# Revit family: Hager-IC-IP40-Transparent_Door-syst-PL-en
name_source: partatom
category: Electrical Equipment
units: mm (PartAtom-declared; Revit-internal decimal feet)

## family parameters
Cut with Voids When Loaded = No
Host = Face
Panel Configuration = Two Columns, Circuits Across
Part Type = Panelboard
Room Calculation Point = No
Round Connector Dimension = Use Diameter
Shared = No

## types (2) — shared parameters
EF000007 - Colour = EV000202 - White
EF000116 - RAL-number = 9010
EF000118 - With mounting plate = No
EF000266 - Number of rows = 2
EF000339 - Type of cover = EV004216 - Door
EF001062 - EMC-version = No
EF001088 - Extension possible = Yes
EF001131 - Internal depth = 72 mm  [stored 0.23622 ft]
EF001134 - DIN-rail = Yes
EF001596 - Material housing = EV000139 - Plastic
EF002950 - Width in number of modular spacings = 12
EF004462 - Type of closure = EV000154 - Other
EF005474 - Degree of protection (IP) = EV006415 - IP40
EF006244 - Transparent cover/door = Yes
EF006306 - With lock = No
EF009212 - Cover model = EV000116 - Closed
EF015776 - Earthing terminal block = Yes
EF015777 - Neutral terminal block = Yes
EF015941 - Signal passing door = Yes
HG000001 - Number of columns = 1
HG000002 - With door or cover = Yes
HG000003 - Range = IC
HG000005 - Thickness = 3 mm  [stored 0.00984252 ft]
HG000009 - Double swing door = No
HG000010 - Asymmetric doors = No
HG000011 - Empty rows from bottom = No
HG000017 - Distance between poles = 18 mm  [stored 0.0590551 ft]
Manufacturer = Hager
Type Comments = IC
zero-valued in all types: Default Elevation, HG000007 - Number of empty columns, HG000008 - Number of empty rows

## per-type parameters (varying)
| type | EF000003 - Mounting method | EF000008 - Width | EF000040 - Height | EF000049 - Depth | EF000218 - Built-in depth | EF000332 - Built-in height | EF000846 - Built-in width | HG000004 - Manufacturer reference | HG000006 - Flush mounted | Model |
| Recessed mounted IP40 W308 H351 D93 12 Modular spacings - VR212TP | EV000383 - Flush mounted (plaster) | 308 mm | 351 mm | 93 mm | 72 mm  [stored 0.23622 ft] | 333 mm | 290 mm | VR212TP | Yes | VR212TP |
| Surface mounted IP40 W294 H326.5 D92.5 12 Modular spacings - VD212TP | EV000384 - Surface mounted (plaster) | 294 mm  [stored 0.964567 ft] | 326 mm  [stored 1.06955 ft] | 92 mm  [stored 0.301837 ft] | 0 mm  [stored 0 ft] | 0 mm  [stored 0 ft] | 0 mm  [stored 0 ft] | VD212TP | No | VD212TP |

note: [stored X ft] marks values corroborated as IEEE doubles in the binary element streams (Revit-internal decimal feet)

## geometry (parser evidence)
native form markers: Sweep x17
no freeform markers — native parametric forms only
